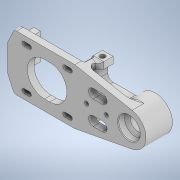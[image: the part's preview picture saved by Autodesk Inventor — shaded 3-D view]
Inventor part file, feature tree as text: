
AUTODESK INVENTOR PART (.ipt)
format: ipt  version: 2020 (Build 240168000, 168)  size: 713,728 bytes
history: native  units: in
note: dims shown in document units (in); Inventor stores cm internally (conversion verified against a paired STEP export)
features: extrude x21, sketch x21, projected_geometry x21, fillet x12, chamfer x5, reference x3, other x3, thicken_offset x2
ambient origin geometry x8: Origin, YZ Plane, XZ Plane, XY Plane, X Axis, Y Axis, Z Axis, Center Point
bodies: Solid1 (feature_tree)
feature tree (88):
  extrude  "Extrusion1"  Depth=1.6535in
  extrude  "Extrusion2"  Depth=1.6535in
  extrude  "Extrusion3"  Depth=0.1969in
  extrude  "Extrusion4"  Depth=0.1969in
  extrude  "Extrusion5"  Depth=0.5906in TaperAngle=0.0deg
  extrude  "Extrusion6"  Depth=0.315in
  extrude  "Extrusion7"  Depth=0.5906in TaperAngle=0.0deg
  chamfer  "Chamfer1"  Distance=0.1969in
  extrude  "Extrusion8"  Depth=0.1969in
  extrude  "Extrusion9"  Depth=0.7874in TaperAngle=45.0deg
  extrude  "Extrusion10"  Depth=0.126in
  chamfer  "Chamfer2"  Distance=0.7874in
  fillet  "Fillet1"  Radius=1.0236in
  fillet  "Fillet2"  Radius=0.7874in
  fillet  "Fillet3"  Radius=0.0787in
  fillet  "Fillet4"  Radius=1.0236in
  extrude  "Extrusion11"  Depth=0.7874in TaperAngle=45.0deg
  extrude  "Extrusion12"  Depth=0.0591in
  extrude  "Extrusion13"  Depth=0.1575in
  chamfer  "Chamfer3"  Distance=0.1378in
  extrude  "Extrusion14"  Depth=0.1181in
  fillet  "Fillet5"  Radius=0.0394in
  fillet  "Fillet6"  Radius=0.1378in
  chamfer  "Chamfer4"  Distance=0.2756in
  fillet  "Fillet7"  Radius=0.7874in
  fillet  "Fillet8"  Radius=0.1969in
  extrude  "Extrusion15"  Depth=0.1181in
  fillet  "Fillet9"  Radius=0.7874in
  extrude  "Extrusion16"  Depth=0.1181in
  extrude  "Extrusion17"  Depth=0.1181in
  extrude  "Extrusion18"  Depth=0.1969in
  extrude  "Extrusion19"  Depth=0.1181in TaperAngle=0.0deg
  fillet  "Fillet10"  Radius=0.1575in
  extrude  "Extrusion20"  Depth=0.1181in
  extrude  "Extrusion21"  Depth=0.1181in
  fillet  "Fillet11"  Radius=0.2756in
  fillet  "Fillet12"  Radius=0.1575in
  thicken_offset  "Thicken1"
  thicken_offset  "Thicken2"
  chamfer  "Chamfer5"  Distance=0.0394in
  sketch  "Sketch1"  dims[d0=2.4409in d1=1.6535in]
  reference  "Reference1"
  sketch  "Sketch2"  dims[d2=1.6535in d3=1.0236in]
  projected_geometry  "Projected Loop1"
  sketch  "Sketch3"  dims[d4=0.1969in d5=0.0in d6=1.0236in]
  projected_geometry  "Projected Loop2"
  reference  "Reference2"
  sketch  "Sketch4"  dims[d7=0.5906in d8=0.0in d9=0.1969in]
  projected_geometry  "Projected Loop3"
  projected_geometry  "Projected Loop4"
  projected_geometry  "Projected Loop5"
  sketch  "Sketch5"  dims[d10=1.6535in d11=0.5906in d12=0.0in]
  projected_geometry  "Projected Loop6"
  sketch  "Sketch6"  dims[d13=0.8661in d14=0.315in]
  sketch  "Sketch7"  dims[d15=1.1811in d16=0.5906in d17=0.0in]
  projected_geometry  "Projected Loop7"
  sketch  "Sketch8"  dims[d18=0.6299in d19=0.1969in d20=0.0in]
  projected_geometry  "Projected Loop8"
  sketch  "Sketch9"  dims[d21=0.1969in d22=0.0in d23=0.4724in]
  projected_geometry  "Projected Loop9"
  sketch  "Sketch10"  dims[d24=0.7874in d25=0.0in d26=0.0787in d27=0.0787in d28=45.0deg]
  projected_geometry  "Projected Loop10"
  sketch  "Sketch11"  dims[d29=0.0787in d30=0.126in]
  projected_geometry  "Projected Loop11"
  projected_geometry  "Projected Loop12"
  sketch  "Sketch12"  dims[d31=0.0787in]
  projected_geometry  "Projected Loop13"
  sketch  "Sketch13"  dims[d32=0.126in]
  projected_geometry  "Projected Loop14"
  sketch  "Sketch14"  dims[d33=0.0787in]
  projected_geometry  "Projected Loop15"
  sketch  "Sketch15"  dims[d34=0.126in]
  projected_geometry  "Projected Loop16"
  sketch  "Sketch16"  dims[d35=0.0787in]
  projected_geometry  "Projected Loop17"
  sketch  "Sketch17"  dims[d36=0.126in d37=0.7874in d38=0.0in d39=1.0236in d40=0.7874in d41=0.0in d42=0.0787in d43=1.0236in]
  projected_geometry  "Projected Loop18"
  sketch  "Sketch18"  dims[d44=0.7874in d45=0.0in d46=0.0787in d47=0.0787in d48=45.0deg]
  reference  "Reference3"
  projected_geometry  "Projected Loop19"
  sketch  "Sketch19"  dims[d49=0.0591in d50=0.1575in]
  projected_geometry  "Projected Loop20"
  sketch  "Sketch20"  dims[d51=0.1575in d52=0.1575in]
  projected_geometry  "Projected Loop21"
  sketch  "Sketch21"  dims[d53=0.0394in d54=0.1378in d55=0.2756in d56=0.0394in d57=0.1378in d58=0.2756in d59=0.7874in d60=0.0in d61=0.1969in d62=0.1575in d63=0.7874in d64=0.0in d65=0.0787in d66=0.4724in d67=0.1969in d68=0.2756in d69=0.0in d70=0.1575in d71=0.0787in d72=45.0deg d73=0.1181in d74=0.2756in d75=0.2756in d76=0.0in d77=0.1575in d78=0.0394in d79=0.0394in d80=0.0787in d81=45.0deg d82=0.0394in d83=0.0787in d84=0.1575in d85=0.1575in d86=0.1969in d87=0.0in d88=0.0394in d89=0.6693in d90=0.5906in d91=0.1181in d92=0.1181in d93=1.1811in d94=0.0in d95=0.1575in d96=1.6535in d97=0.1969in d98=0.0in d99=0.3937in d100=0.1969in d101=0.7874in d102=0.7874in d103=0.0in d104=0.1969in d105=0.0in d106=0.315in d107=0.2362in d108=0.2362in d109=0.1575in d110=0.1575in d111=0.1969in d112=0.0in d113=0.1575in d114=0.1969in d115=0.0in d116=0.0394in d117=0.1181in d118=0.0059in d119=0.0059in d120=0.0059in d121=0.0059in d122=0.0197in d123=0.0787in d124=45.0deg]
  parser-record x1  (decoder bookkeeping rows leaked as tree rows — omitted from the tree; the rows remain in map.json)
  other  "arm_shift_1.iam"
  other  "Nema17 Stepper Motor:1"
note: 1 file-system path scrubbed to <path> (originals preserved in map.json)
